# Revit family: HL Трап для внутренних помещенийHL310NPr-SML
name_source: partatom
category: Сантехнические приборы
units: mm (PartAtom-declared; Revit-internal decimal feet)

## family parameters
Всегда вертикально = Да
Заголовок OmniClass = Deck Waste Water Drains
На основе рабочей плоскости = Нет
Номер OmniClass = 23.70.50.21.24.14
Общий = Да
Отображать на видах в сечении = Нет
При загрузке вырезать с полостями = Нет
Размер круглого соединителя = Использовать диаметр
Сохранять ориентацию аннотаций = Нет
Тип детали = Нормальный
Точка принадлежности помещению = Да

## types (1)
- HL310KSML_50
    EAN = 9003076004638
    URL = http://www.hutterer-lechner.com
    ВЕС = 0,72 [kg]
    ВЫСОТА МОНТАЖА = 163 mm
    Изготовитель = HL Hutterer & Lechner GmbH
    Ключевая пометка = HL310KSML_50
    Комментарии к типоразмеру = Корпус трапа для внутренних помещений DN50/75/110 вертикальный
    МАКСИМАЛЬНАЯ НАГРУЗКА КЛАССА = K3 - 300 kg
    МАТЕРИАЛ = PP, V2A
    Модель = HL310KSML_50
    НАСАДКА = 12-70 mm / 123 x 123 mm / PP
    Нормы = EN 1253-1
    Описание = Трап для внутренних помещений
    Отметка по умолчанию = 0 мм
    ПРОИЗВОДИТЕЛЬНОСТЬ = 0,67 l/s
    ПРОПУСКНАЯ СПОСОБНОСТЬ = 0.7 л/с
    Подключение к вентиляции = Нет
    Подключение к горячей воде = Нет
    Подключение к сливной трубе = Да
    Подключение к холодной воде = Нет
    РАЗМЕР = DN50/75/110
    РЕШЁТКА = 115 x 115 mm / V2A

## geometry (parser evidence)
native form markers: Sweep x78
no freeform markers — native parametric forms only
